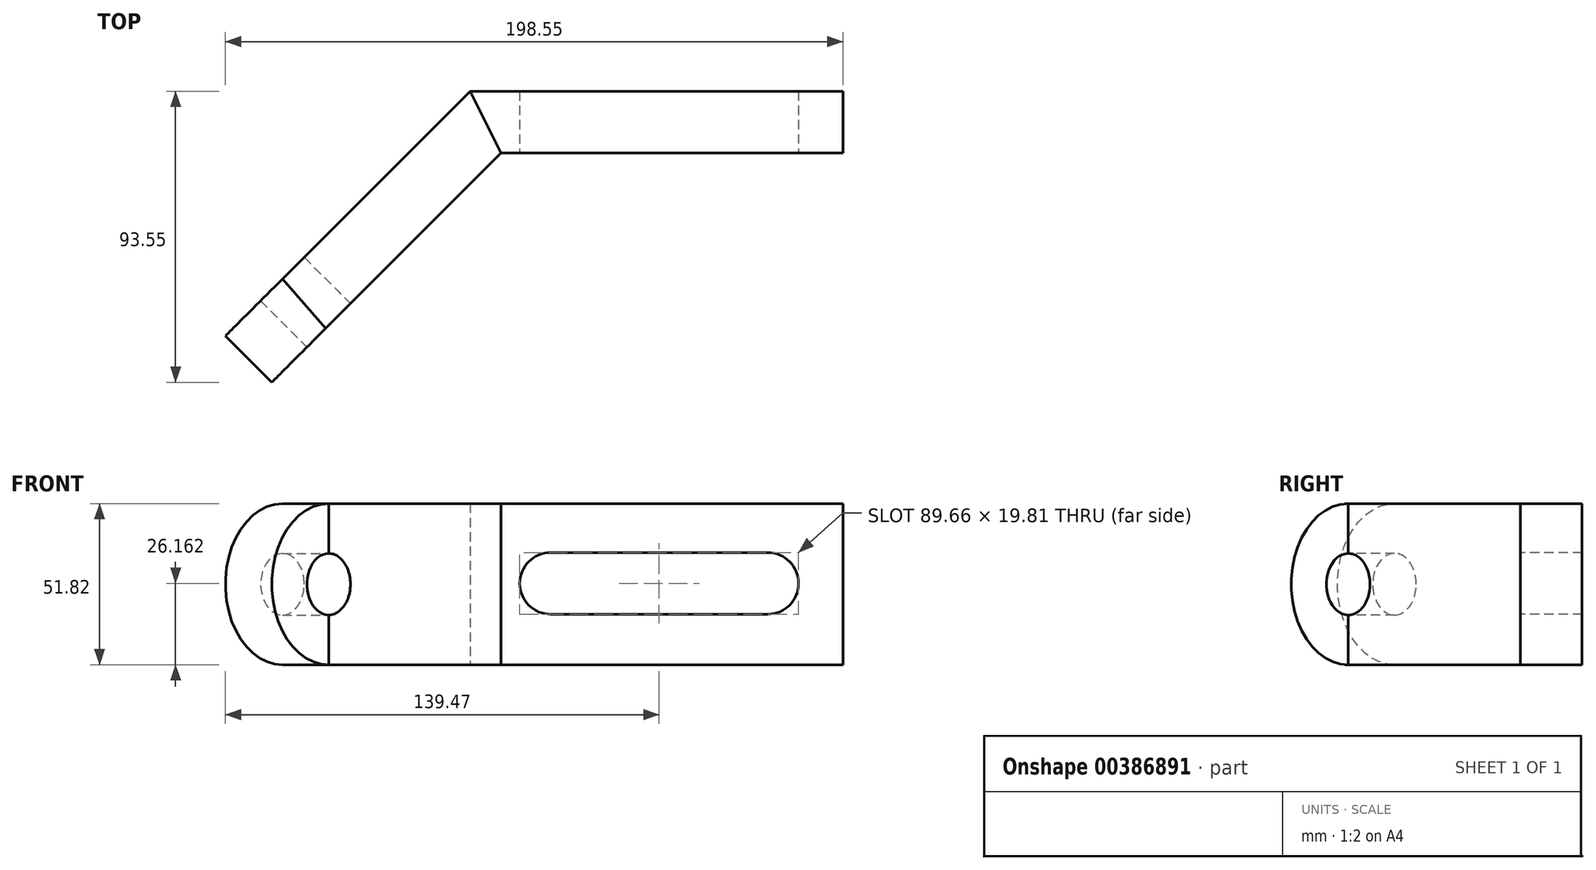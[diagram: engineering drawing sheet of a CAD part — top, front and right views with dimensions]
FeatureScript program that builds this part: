
annotation { "Feature Type Name" : "Feature", "Feature Type Description" : "" }
export const myFeature = defineFeature(function(context is Context, id is Id, definition is map)
    precondition{}
    {
        {
            var Q0;
            Q0=qCreatedBy(makeId("Front.planeOp"),FACE);
            var sketch = newSketch(context, id + "F0", { "sketchPlane" : qUnion([Q0])});
            skLineSegment(sketch, "E0.bottom", {"start": v(0, 0) * mm, "end": v(-119.89, 0) * mm});
            skLineSegment(sketch, "E0.top", {"start": v(0, 51.82) * mm, "end": v(-119.89, 51.82) * mm});
            skLineSegment(sketch, "E0.left", {"start": v(0, 0) * mm, "end": v(0, 51.82) * mm});
            skLineSegment(sketch, "E0.right", {"start": v(-119.89, 0) * mm, "end": v(-119.89, 51.82) * mm});
            skSolve(sketch);
        }
        {
            var Q0;
            Q0 = qSketchRegion(id + "F0", true);
            extrude(context, id + "F1", {"entities" : qUnion([Q0]), "depth" : 9.9 * mm});
        }
        {
            var Q0;
            Q0=makeQuery(id+"F1.opExtrude","CAP_FACE",FACE,{"disambiguationData":[OSD([sQuery(id+"F0.wireOp",EDGE,"E0.bottom"),sQuery(id+"F0.wireOp",EDGE,"E0.top"),sQuery(id+"F0.wireOp",EDGE,"E0.left"),sQuery(id+"F0.wireOp",EDGE,"E0.right")])],"isStart":false});
            var sketch = newSketch(context, id + "F2", { "sketchPlane" : qUnion([Q0])});
            skLineSegment(sketch, "E1.bottom", {"start": v(0, 0) * mm, "end": v(-109.98, 0) * mm});
            skLineSegment(sketch, "E1.top", {"start": v(0, 51.82) * mm, "end": v(-109.98, 51.82) * mm});
            skLineSegment(sketch, "E1.left", {"start": v(0, 0) * mm, "end": v(0, 51.82) * mm});
            skLineSegment(sketch, "E1.right", {"start": v(-109.98, 0) * mm, "end": v(-109.98, 51.82) * mm});
            skSolve(sketch);
        }
        {
            var Q0;
            Q0 = qSketchRegion(id + "F2", true);
            extrude(context, id + "F3", {"entities" : qUnion([Q0]), "operationType" : NewBodyOperationType.ADD, "depth" : 9.9 * mm});
        }
        {
            var Q0;
            Q0=makeQuery(id+"F3.boolean.opBoolean","MERGE",FACE,{"derivedFrom":[makeQuery(id+"F1.opExtrude","SWEPT_FACE",FACE,{"disambiguationData":[OSD([sQuery(id+"F0.wireOp",EDGE,"E0.bottom")])]}),makeQuery(id+"F3.opExtrude","SWEPT_FACE",FACE,{"disambiguationData":[OSD([sQuery(id+"F2.wireOp",EDGE,"E1.bottom")])]})]});
            var sketch = newSketch(context, id + "F4", { "sketchPlane" : qUnion([Q0])});
            skLineSegment(sketch, "E2", {"start": v(-109.98, 19.81) * mm, "end": v(-119.89, 9.9) * mm});
            skSolve(sketch);
        }
        {
            var Q0;
            Q0=makeQuery(id+"F4.imprint","IMPRINT",FACE,{"disambiguationData":[TD([[makeQuery(id+"F4.imprint","IMPRINT",EDGE,{"derivedFrom":sQuery(id+"F4.wireOp",EDGE,"E2")}),1.0]])]});
            extrude(context, id + "F5", {"entities" : qUnion([Q0]), "operationType" : NewBodyOperationType.ADD, "oppositeDirection" : true, "depth" : 51.82 * mm});
        }
        {
            var Q0;
            {var subQ0=sQuery(id+"F2.wireOp",EDGE,"E1.bottom");var subQ1=sQuery(id+"F0.wireOp",EDGE,"E0.bottom");Q0=makeQuery(id+"F5.boolean.opBoolean","MERGE",FACE,{"derivedFrom":[makeQuery(id+"F3.boolean.opBoolean","MERGE",FACE,{"derivedFrom":[makeQuery(id+"F1.opExtrude","SWEPT_FACE",FACE,{"disambiguationData":[OSD([subQ1])]}),makeQuery(id+"F3.opExtrude","SWEPT_FACE",FACE,{"disambiguationData":[OSD([subQ0])]})]}),makeQuery(id+"F5.opExtrude","CAP_FACE",FACE,{"disambiguationData":[OSD([subQ1,subQ0,sQuery(id+"F2.wireOp",EDGE,"E1.right"),sQuery(id+"F4.wireOp",EDGE,"E2")])],"isStart":true})]});}
            var sketch = newSketch(context, id + "F6", { "sketchPlane" : qUnion([Q0])});
            skLineSegment(sketch, "E3", {"start": v(-109.98, 19.81) * mm, "end": v(-119.89, 0) * mm});
            skSolve(sketch);
        }
        {
            var Q0;
            Q0=makeQuery(id+"F6.imprint","IMPRINT",FACE,{"disambiguationData":[TD([[makeQuery(id+"F6.imprint","IMPRINT",EDGE,{"derivedFrom":sQuery(id+"F6.wireOp",EDGE,"E3")}),-1.0]])]});
            extrude(context, id + "F7", {"entities" : qUnion([Q0]), "operationType" : NewBodyOperationType.REMOVE, "oppositeDirection" : true, "depth" : 51.82 * mm});
        }
        {
            var Q0;
            {var subQ0=sQuery(id+"F2.wireOp",EDGE,"E1.bottom");var subQ1=sQuery(id+"F0.wireOp",EDGE,"E0.bottom");Q0=makeQuery(id+"F5.boolean.opBoolean","MERGE",FACE,{"derivedFrom":[makeQuery(id+"F3.boolean.opBoolean","MERGE",FACE,{"derivedFrom":[makeQuery(id+"F1.opExtrude","SWEPT_FACE",FACE,{"disambiguationData":[OSD([subQ1])]}),makeQuery(id+"F3.opExtrude","SWEPT_FACE",FACE,{"disambiguationData":[OSD([subQ0])]})]}),makeQuery(id+"F5.opExtrude","CAP_FACE",FACE,{"disambiguationData":[OSD([subQ1,subQ0,sQuery(id+"F2.wireOp",EDGE,"E1.right"),sQuery(id+"F4.wireOp",EDGE,"E2")])],"isStart":true})]});}
            var sketch = newSketch(context, id + "F8", { "sketchPlane" : qUnion([Q0])});
            skLineSegment(sketch, "E4", {"start": v(-109.98, 19.81) * mm, "end": v(-166.38, 76.2) * mm});
            skLineSegment(sketch, "E5", {"start": v(-119.89, 0) * mm, "end": v(-180.23, 60.34) * mm});
            skLineSegment(sketch, "E6", {"start": v(-166.38, 76.2) * mm, "end": v(-180.23, 60.34) * mm});
            skSolve(sketch);
        }
        {
            var Q0;
            Q0=makeQuery(id+"F8.imprint","IMPRINT",FACE,{"disambiguationData":[TD([[makeQuery(id+"F8.imprint","IMPRINT",EDGE,{"derivedFrom":sQuery(id+"F8.wireOp",EDGE,"E4")}),1.0]])]});
            extrude(context, id + "F9", {"entities" : qUnion([Q0]), "oppositeDirection" : true, "depth" : 51.82 * mm});
        }
        {
            var Q0;
            Q0=makeQuery(id+"F9.opExtrude","SWEPT_FACE",FACE,{"disambiguationData":[OSD([sQuery(id+"F8.wireOp",EDGE,"E5")])]});
            var sketch = newSketch(context, id + "F10", { "sketchPlane" : qUnion([Q0])});
            skArc(sketch, "E7", {"start": v(170.1, 0) * mm, "mid": v(196.01, 25.9) * mm, "end": v(170.1, 51.82) * mm});
            skSolve(sketch);
        }
        {
            var Q0;
            Q0=makeQuery(id+"F10.imprint","IMPRINT",FACE,{"disambiguationData":[TD([[makeQuery(id+"F10.imprint","IMPRINT",EDGE,{"derivedFrom":sQuery(id+"F10.wireOp",EDGE,"E7")}),1.0]])]});
            extrude(context, id + "F11", {"entities" : qUnion([Q0]), "operationType" : NewBodyOperationType.ADD, "oppositeDirection" : true, "depth" : 21.06 * mm});
        }
        {
            var Q0;
            Q0=makeQuery(id+"F3.opExtrude","CAP_FACE",FACE,{"disambiguationData":[OSD([sQuery(id+"F2.wireOp",EDGE,"E1.bottom"),sQuery(id+"F2.wireOp",EDGE,"E1.top"),sQuery(id+"F2.wireOp",EDGE,"E1.left"),sQuery(id+"F2.wireOp",EDGE,"E1.right")])],"isStart":false});
            var sketch = newSketch(context, id + "F12", { "sketchPlane" : qUnion([Q0])});
            skLineSegment(sketch, "E8.bottom", {"start": v(-94, 36.07) * mm, "end": v(-24.16, 36.07) * mm});
            skLineSegment(sketch, "E8.top", {"start": v(-94, 16.26) * mm, "end": v(-24.16, 16.26) * mm});
            skLineSegment(sketch, "E8.left", {"start": v(-94, 36.07) * mm, "end": v(-94, 16.26) * mm});
            skLineSegment(sketch, "E8.right", {"start": v(-24.16, 36.07) * mm, "end": v(-24.16, 16.26) * mm});
            skArc(sketch, "E9", {"start": v(-24.16, 16.26) * mm, "mid": v(-14.25, 26.16) * mm, "end": v(-24.16, 36.07) * mm});
            skArc(sketch, "E10", {"start": v(-94, 36.07) * mm, "mid": v(-103.91, 26.16) * mm, "end": v(-94, 16.26) * mm});
            skSolve(sketch);
        }
        {
            var Q0;
            Q0=makeQuery(id+"F12.imprint","IMPRINT",FACE,{"disambiguationData":[TD([[makeQuery(id+"F12.imprint","IMPRINT",EDGE,{"derivedFrom":sQuery(id+"F12.wireOp",EDGE,"E8.bottom")}),-1.0]])]});
            var Q1;
            Q1=makeQuery(id+"F12.imprint","IMPRINT",FACE,{"disambiguationData":[TD([[makeQuery(id+"F12.imprint","IMPRINT",EDGE,{"derivedFrom":sQuery(id+"F12.wireOp",EDGE,"E8.left")}),-1.0]])]});
            var Q2;
            Q2=makeQuery(id+"F12.imprint","IMPRINT",FACE,{"disambiguationData":[TD([[makeQuery(id+"F12.imprint","IMPRINT",EDGE,{"derivedFrom":sQuery(id+"F12.wireOp",EDGE,"E8.right")}),1.0]])]});
            extrude(context, id + "F13", {"entities" : qUnion([Q0, Q1, Q2]), "operationType" : NewBodyOperationType.REMOVE, "oppositeDirection" : true, "depth" : 19.8 * mm});
        }
        {
            var Q0;
            Q0=makeQuery(id+"F11.opExtrude","CAP_FACE",FACE,{"disambiguationData":[OSD([sQuery(id+"F8.wireOp",EDGE,"E5"),sQuery(id+"F8.wireOp",EDGE,"E6"),sQuery(id+"F10.wireOp",EDGE,"E7")])],"isStart":false});
            var sketch = newSketch(context, id + "F14", { "sketchPlane" : qUnion([Q0])});
            skCircle(sketch, "E11", {"center": v(-170.1, 25.9) * mm, "radius": 9.9 * mm});
            skSolve(sketch);
        }
        {
            var Q0;
            Q0 = qSketchRegion(id + "F14", true);
            extrude(context, id + "F15", {"entities" : qUnion([Q0]), "operationType" : NewBodyOperationType.REMOVE, "oppositeDirection" : true, "depth" : 25.4 * mm});
        }
    });
